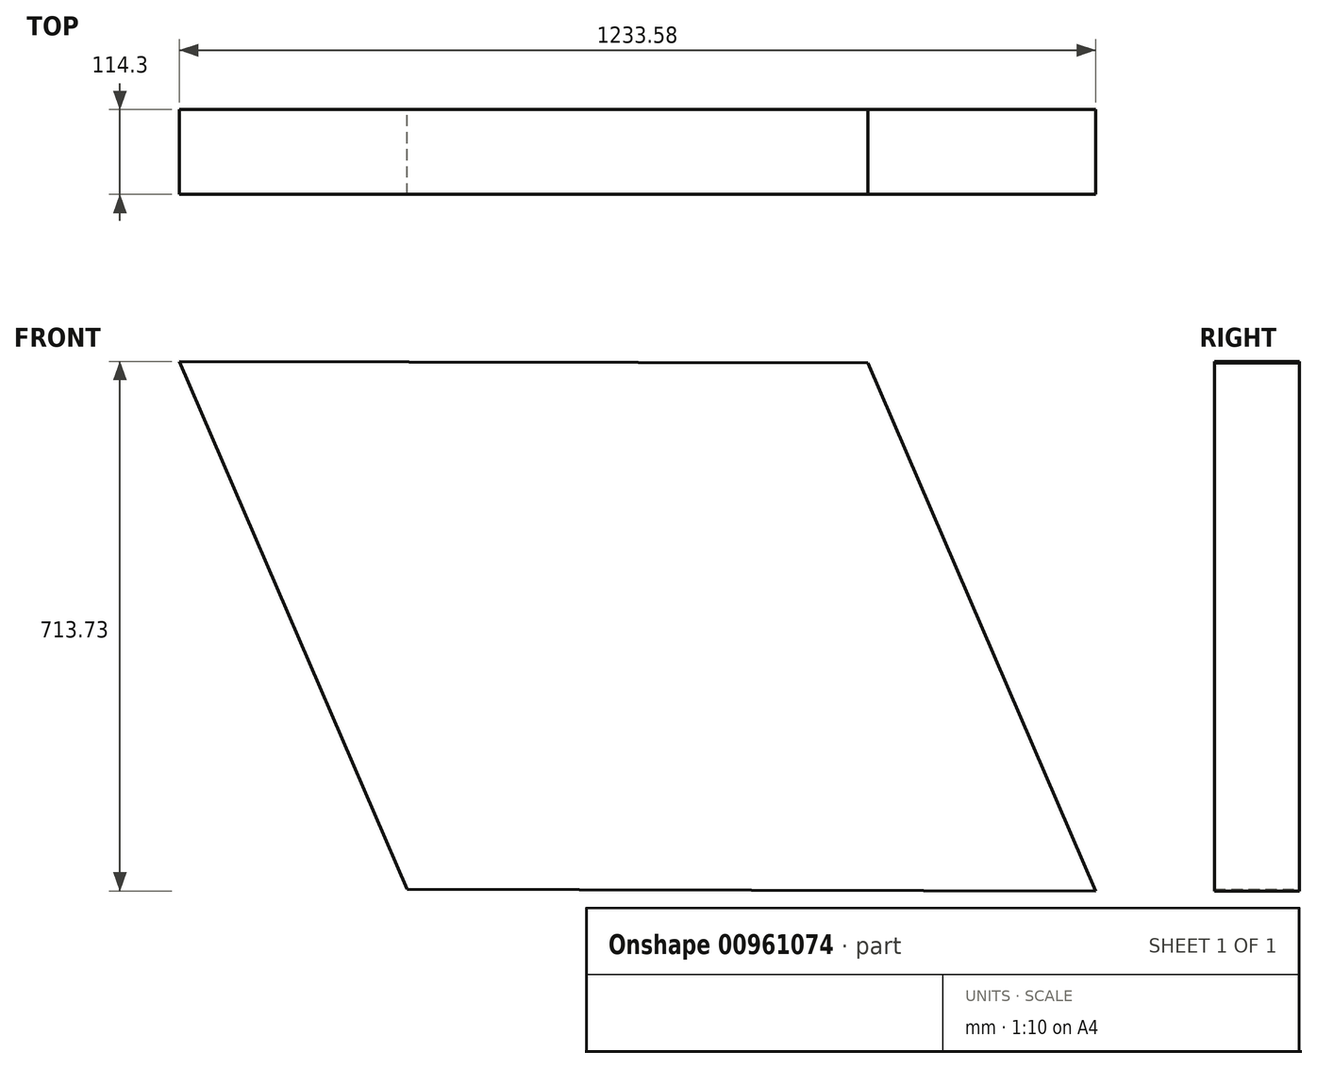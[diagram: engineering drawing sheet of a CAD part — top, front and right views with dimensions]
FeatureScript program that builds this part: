
annotation { "Feature Type Name" : "Feature", "Feature Type Description" : "" }
export const myFeature = defineFeature(function(context is Context, id is Id, definition is map)
    precondition{}
    {
        {
            var Q0;
            Q0=qCreatedBy(makeId("Front.planeOp"),FACE);
            var sketch = newSketch(context, id + "F0", { "sketchPlane" : qUnion([Q0])});
            skLineSegment(sketch, "E0.bottom", {"start": v(-584.5, 370.84) * mm, "end": v(342.6, 368.6) * mm});
            skLineSegment(sketch, "E0.top", {"start": v(-278.01, -340.66) * mm, "end": v(649.09, -342.9) * mm});
            skLineSegment(sketch, "E0.left", {"start": v(-584.5, 370.84) * mm, "end": v(-278.01, -340.66) * mm});
            skLineSegment(sketch, "E0.right", {"start": v(342.6, 368.6) * mm, "end": v(649.09, -342.9) * mm});
            skSolve(sketch);
        }
        {
            var Q0;
            Q0=makeQuery(id+"F0.imprint","IMPRINT",FACE,{"disambiguationData":[TD([[makeQuery(id+"F0.imprint","IMPRINT",EDGE,{"derivedFrom":sQuery(id+"F0.wireOp",EDGE,"E0.bottom")}),-1.0]])]});
            extrude(context, id + "F1", {"entities" : qUnion([Q0]), "depth" : 114.3 * mm, "offsetDistance" : 25.4 * mm});
        }
    });
